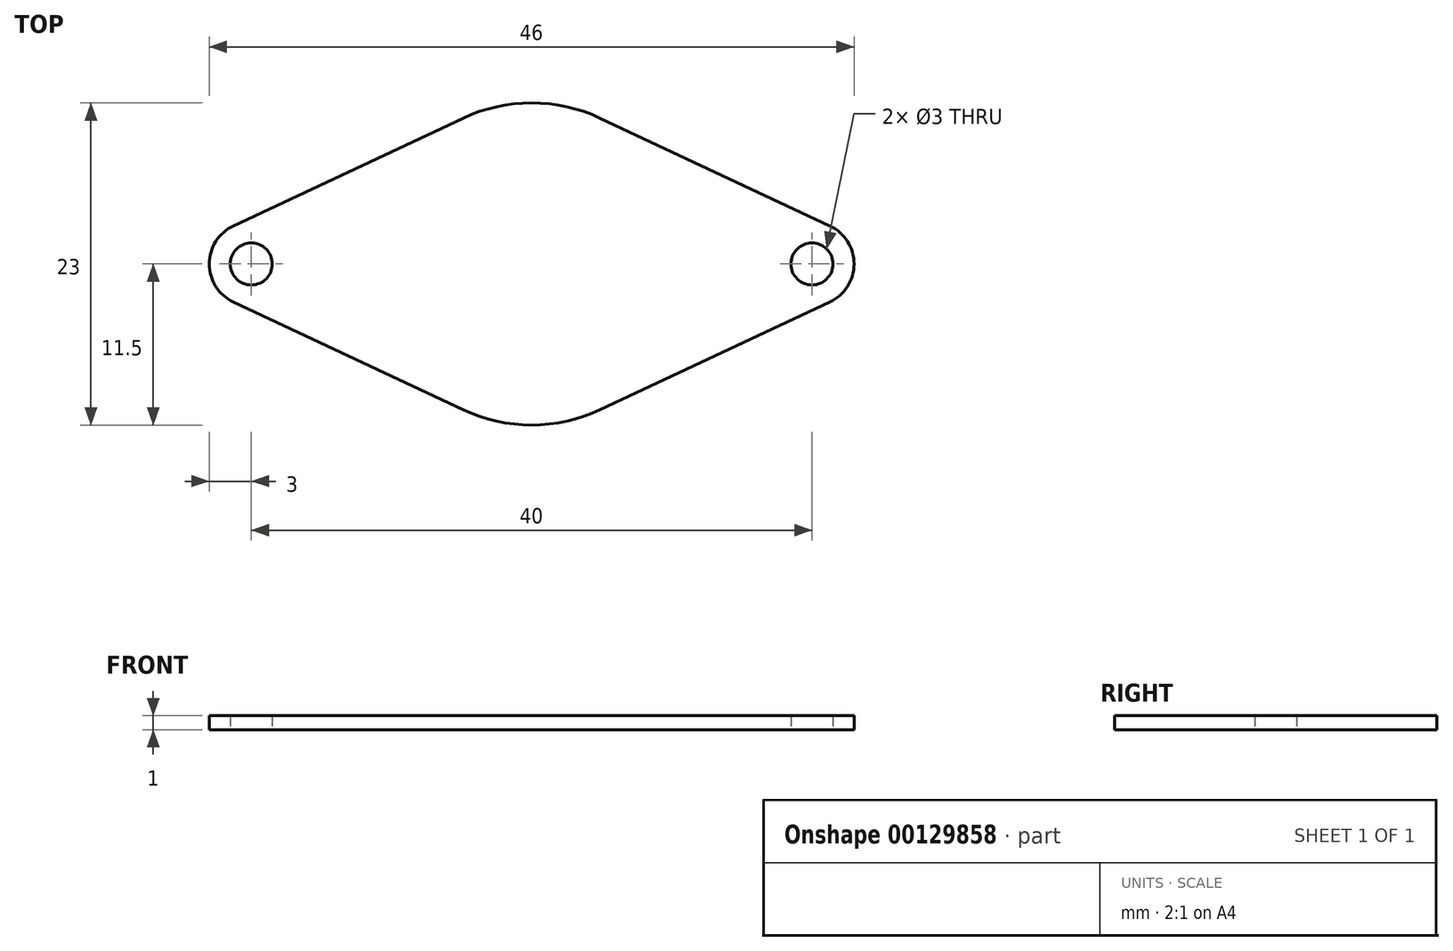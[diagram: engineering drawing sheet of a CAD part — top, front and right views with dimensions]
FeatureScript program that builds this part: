
annotation { "Feature Type Name" : "Feature", "Feature Type Description" : "" }
export const myFeature = defineFeature(function(context is Context, id is Id, definition is map)
    precondition{}
    {
        {
            var Q0;
            Q0=qCreatedBy(makeId("Top.planeOp"),FACE);
            var sketch = newSketch(context, id + "F0", { "sketchPlane" : qUnion([Q0])});
            skCircle(sketch, "E0", {"center": v(0.06, 0.01) * mm, "radius": 8.5 * mm});
            skCircle(sketch, "E1.0", {"center": v(0.06, 0.01) * mm, "radius": 11.5 * mm});
            skLineSegment(sketch, "E2", {"start": v(0.06, 0.01) * mm, "end": v(-19.94, 0.01) * mm, "construction": true});
            skLineSegment(sketch, "E3", {"start": v(0.06, 0.01) * mm, "end": v(20.06, 0.01) * mm, "construction": true});
            skCircle(sketch, "E4", {"center": v(-19.94, 0.01) * mm, "radius": 1.5 * mm});
            skCircle(sketch, "E5", {"center": v(-19.94, 0.01) * mm, "radius": 3 * mm});
            skCircle(sketch, "E6", {"center": v(20.06, 0.01) * mm, "radius": 1.5 * mm});
            skCircle(sketch, "E7", {"center": v(20.06, 0.01) * mm, "radius": 3 * mm});
            skLineSegment(sketch, "E8", {"start": v(-21.21, 2.73) * mm, "end": v(-4.83, 10.42) * mm});
            skLineSegment(sketch, "E9", {"start": v(21.34, 2.73) * mm, "end": v(4.95, 10.42) * mm});
            skLineSegment(sketch, "E10", {"start": v(-21.21, -2.7) * mm, "end": v(-4.83, -10.4) * mm});
            skLineSegment(sketch, "E11", {"start": v(21.34, -2.7) * mm, "end": v(4.95, -10.4) * mm});
            skSolve(sketch);
        }
        {
            var Q0;
            Q0=makeQuery(id+"F0.imprint","IMPRINT",FACE,{"disambiguationData":[TD([[makeQuery(id+"F0.imprint","IMPRINT",EDGE,{"derivedFrom":sQuery(id+"F0.wireOp",EDGE,"E4")}),-1.0]])]});
            var Q1;
            {var subQ0=sQuery(id+"F0.wireOp",EDGE,"E8");Q1=makeQuery(id+"F0.imprint","IMPRINT",FACE,{"disambiguationData":[TD([[makeQuery(id+"F0.imprint","IMPRINT",EDGE,{"derivedFrom":subQ0}),-1.0]])]});}
            var Q2;
            Q2=makeQuery(id+"F0.imprint","IMPRINT",FACE,{"disambiguationData":[TD([[makeQuery(id+"F0.imprint","IMPRINT",EDGE,{"derivedFrom":sQuery(id+"F0.wireOp",EDGE,"E0")}),-1.0]])]});
            var Q3;
            Q3=makeQuery(id+"F0.imprint","IMPRINT",FACE,{"disambiguationData":[TD([[makeQuery(id+"F0.imprint","IMPRINT",EDGE,{"derivedFrom":sQuery(id+"F0.wireOp",EDGE,"E0")}),1.0]])]});
            var Q4;
            {var subQ0=sQuery(id+"F0.wireOp",EDGE,"E9");Q4=makeQuery(id+"F0.imprint","IMPRINT",FACE,{"disambiguationData":[TD([[makeQuery(id+"F0.imprint","IMPRINT",EDGE,{"derivedFrom":subQ0}),1.0]])]});}
            var Q5;
            Q5=makeQuery(id+"F0.imprint","IMPRINT",FACE,{"disambiguationData":[TD([[makeQuery(id+"F0.imprint","IMPRINT",EDGE,{"derivedFrom":sQuery(id+"F0.wireOp",EDGE,"E6")}),-1.0]])]});
            var Q6;
            Q6=sQuery(id+"F0.wireOp",EDGE,"E0");
            var Q7;
            Q7=sQuery(id+"F0.wireOp",EDGE,"E1.0");
            var Q8;
            Q8=sQuery(id+"F0.wireOp",EDGE,"E4");
            var Q9;
            Q9=sQuery(id+"F0.wireOp",EDGE,"E5");
            var Q10;
            Q10=sQuery(id+"F0.wireOp",EDGE,"E6");
            var Q11;
            Q11=sQuery(id+"F0.wireOp",EDGE,"E7");
            var Q12;
            Q12=sQuery(id+"F0.wireOp",EDGE,"E8");
            var Q13;
            Q13=sQuery(id+"F0.wireOp",EDGE,"E9");
            var Q14;
            Q14=sQuery(id+"F0.wireOp",EDGE,"E10");
            var Q15;
            Q15=sQuery(id+"F0.wireOp",EDGE,"E11");
            extrude(context, id + "F1", {"entities" : qUnion([Q0, Q1, Q2, Q3, Q4, Q5]), "surfaceEntities" : qUnion([Q6, Q7, Q8, Q9, Q10, Q11, Q12, Q13, Q14, Q15]), "depth" : 1 * mm});
        }
    });
